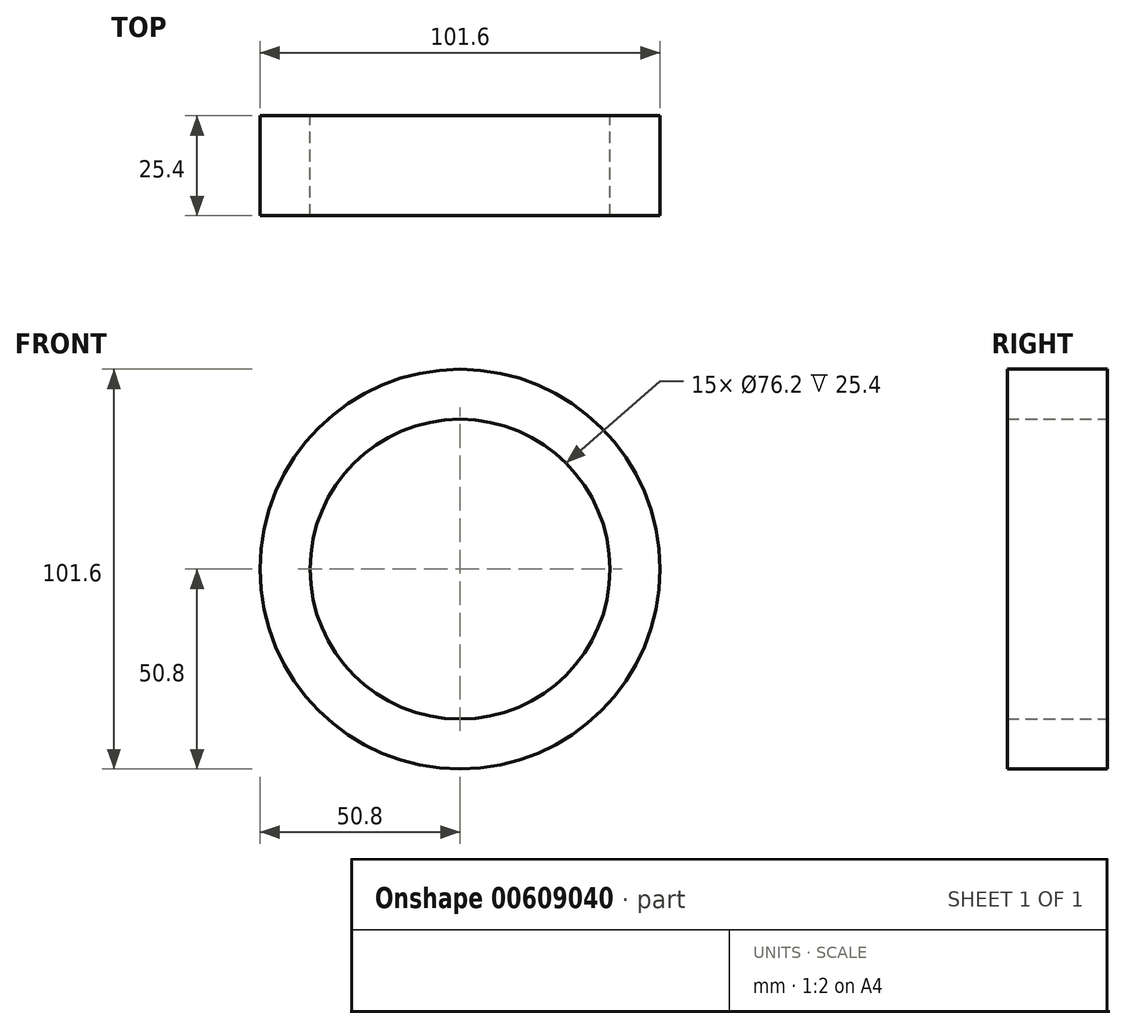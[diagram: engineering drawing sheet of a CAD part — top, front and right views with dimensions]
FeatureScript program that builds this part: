
annotation { "Feature Type Name" : "Feature", "Feature Type Description" : "" }
export const myFeature = defineFeature(function(context is Context, id is Id, definition is map)
    precondition{}
    {
        {
            var Q0;
            Q0=qCreatedBy(makeId("Front.planeOp"),FACE);
            var sketch = newSketch(context, id + "F0", { "sketchPlane" : qUnion([Q0])});
            skCircle(sketch, "E0", {"center": v(0, 0) * mm, "radius": 50.8 * mm});
            skCircle(sketch, "E1", {"center": v(0, 0) * mm, "radius": 38.1 * mm});
            skSolve(sketch);
        }
        {
            var Q0;
            Q0=makeQuery(id+"F0.imprint","IMPRINT",FACE,{"disambiguationData":[TD([[makeQuery(id+"F0.imprint","IMPRINT",EDGE,{"derivedFrom":sQuery(id+"F0.wireOp",EDGE,"E0")}),1.0]])]});
            extrude(context, id + "F1", {"entities" : qUnion([Q0]), "depth" : 25.4 * mm, "offsetDistance" : 25.4 * mm});
        }
    });
